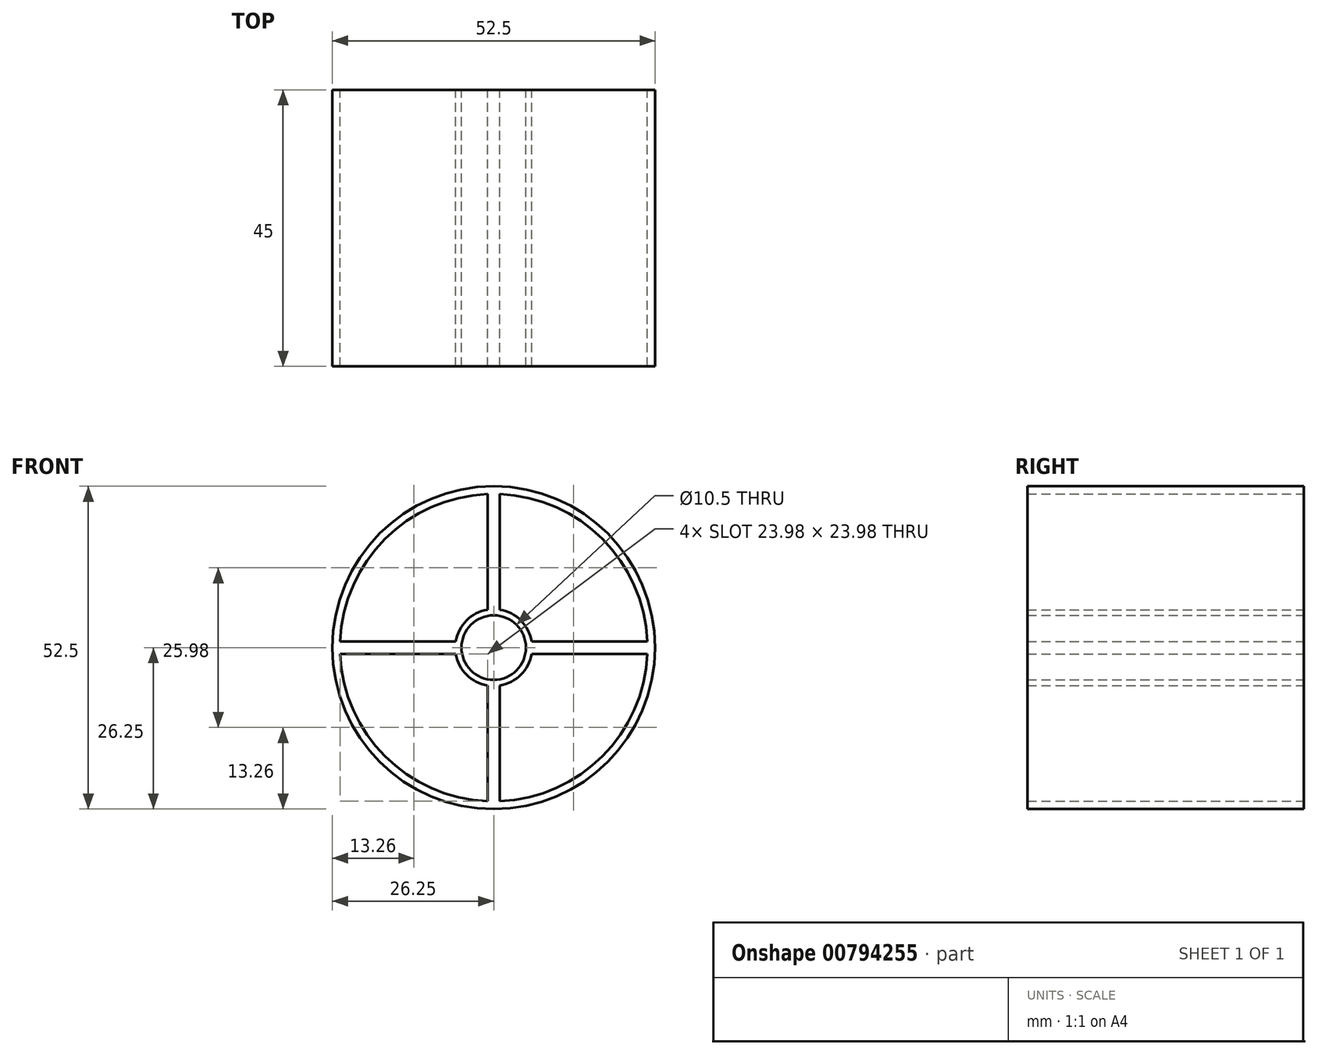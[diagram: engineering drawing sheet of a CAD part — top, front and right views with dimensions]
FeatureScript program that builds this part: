
annotation { "Feature Type Name" : "Feature", "Feature Type Description" : "" }
export const myFeature = defineFeature(function(context is Context, id is Id, definition is map)
    precondition{}
    {
        {
            var Q0;
            Q0=qCreatedBy(makeId("Front.planeOp"),FACE);
            var sketch = newSketch(context, id + "F0", { "sketchPlane" : qUnion([Q0])});
            skArc(sketch, "E0", {"start": v(-5.15, -1) * mm, "mid": v(5.25, 0) * mm, "end": v(-5.15, 1) * mm});
            skCircle(sketch, "E1", {"center": v(0, 0) * mm, "radius": 26.25 * mm});
            skArc(sketch, "E2", {"start": v(-24.98, -1) * mm, "mid": v(-17.68, -17.68) * mm, "end": v(-1, -24.98) * mm});
            skLineSegment(sketch, "E3", {"start": v(-1, 6.17) * mm, "end": v(-1, 24.98) * mm});
            skLineSegment(sketch, "E4", {"start": v(1, 6.17) * mm, "end": v(1, 24.98) * mm});
            skLineSegment(sketch, "E5", {"start": v(-30.26, 0) * mm, "end": v(38.57, 0) * mm, "construction": true});
            skLineSegment(sketch, "E6", {"start": v(0, 31.18) * mm, "end": v(0, -34.63) * mm, "construction": true});
            skLineSegment(sketch, "E7.MirrorCS", {"start": v(-1, -6.17) * mm, "end": v(-1, -24.98) * mm});
            skLineSegment(sketch, "E8.MirrorCS", {"start": v(1, -6.17) * mm, "end": v(1, -24.98) * mm});
            skLineSegment(sketch, "E9", {"start": v(6.17, 1) * mm, "end": v(24.98, 1) * mm});
            skLineSegment(sketch, "E10", {"start": v(6.17, -1) * mm, "end": v(24.98, -1) * mm});
            skLineSegment(sketch, "E11.MirrorCS", {"start": v(-6.17, 1) * mm, "end": v(-24.98, 1) * mm});
            skLineSegment(sketch, "E12.MirrorCS", {"start": v(-6.17, -1) * mm, "end": v(-24.98, -1) * mm});
            skArc(sketch, "E13", {"start": v(1, -6.17) * mm, "mid": v(4.42, -4.42) * mm, "end": v(6.17, -1) * mm});
            skPoint(sketch, "E14.orphan", {"position": v(-1, 5.15) * mm});
            skPoint(sketch, "E15.orphan", {"position": v(1, 5.15) * mm});
            skPoint(sketch, "E16.orphan", {"position": v(5.15, 1) * mm});
            skPoint(sketch, "E17.orphan", {"position": v(5.15, -1) * mm});
            skPoint(sketch, "E18.orphan", {"position": v(1, -5.15) * mm});
            skPoint(sketch, "E19.orphan", {"position": v(-1, -5.15) * mm});
            skPoint(sketch, "E20.orphan", {"position": v(-5.15, -1) * mm});
            skPoint(sketch, "E21.orphan", {"position": v(-5.15, 1) * mm});
            skArc(sketch, "E22.trimOffspring", {"start": v(-1, 24.98) * mm, "mid": v(-17.68, 17.68) * mm, "end": v(-24.98, 1) * mm});
            skArc(sketch, "E23.trimOffspring", {"start": v(24.98, 1) * mm, "mid": v(17.68, 17.68) * mm, "end": v(1, 24.98) * mm});
            skArc(sketch, "E24.trimOffspring", {"start": v(1, -24.98) * mm, "mid": v(17.68, -17.68) * mm, "end": v(24.98, -1) * mm});
            skArc(sketch, "E25.trimOffspring", {"start": v(6.17, 1) * mm, "mid": v(4.42, 4.42) * mm, "end": v(1, 6.17) * mm});
            skArc(sketch, "E26.trimOffspring", {"start": v(-6.17, -1) * mm, "mid": v(-4.42, -4.42) * mm, "end": v(-1, -6.17) * mm});
            skArc(sketch, "E27.trimOffspring", {"start": v(-1, 6.17) * mm, "mid": v(-4.42, 4.42) * mm, "end": v(-6.17, 1) * mm});
            skArc(sketch, "E28", {"start": v(-5.15, 1) * mm, "mid": v(-5.25, 0) * mm, "end": v(-5.15, -1) * mm});
            skSolve(sketch);
        }
        {
            var Q0;
            Q0=makeQuery(id+"F0.imprint","IMPRINT",FACE,{"disambiguationData":[TD([[makeQuery(id+"F0.imprint","IMPRINT",EDGE,{"derivedFrom":sQuery(id+"F0.wireOp",EDGE,"E1")}),1.0]])]});
            extrude(context, id + "F1", {"entities" : qUnion([Q0]), "depth" : 45 * mm, "offsetDistance" : 25 * mm});
        }
    });
